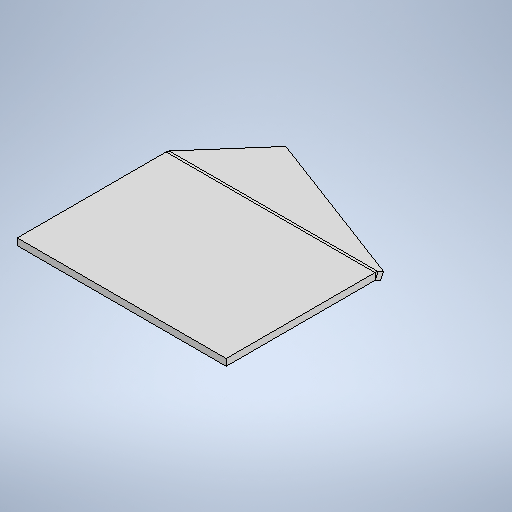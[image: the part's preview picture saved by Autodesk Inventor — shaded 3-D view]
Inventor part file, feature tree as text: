
AUTODESK INVENTOR PART (.ipt)
format: ipt  version: 2025 (Build 290162010, 162A)  size: 283,648 bytes
history: native  units: mm
features: sheet_metal_op x2, sketch x2, other x2, projected_geometry x1
ambient origin geometry x8: Origin, YZ Plane, XZ Plane, XY Plane, X Axis, Y Axis, Z Axis, Center Point
bodies: Body1 (feature_tree)
feature tree (7):
  sheet_metal_op  "Face2"
  sheet_metal_op  "Fold1"
  sketch  "Sketch3"  dims[d18=10.0mm]
  other  "Plate3"
  sketch  "Sketch4"  dims[d19=310.0mm d22=10.0mm d23=10.0mm d24=5.0mm d25=20.0mm d26=10.0mm d27=4.363323mm d28=1.0mm d29=232.0mm d30=182.0mm]
  projected_geometry  "Projected Loop1"
  other  "Definition1"
